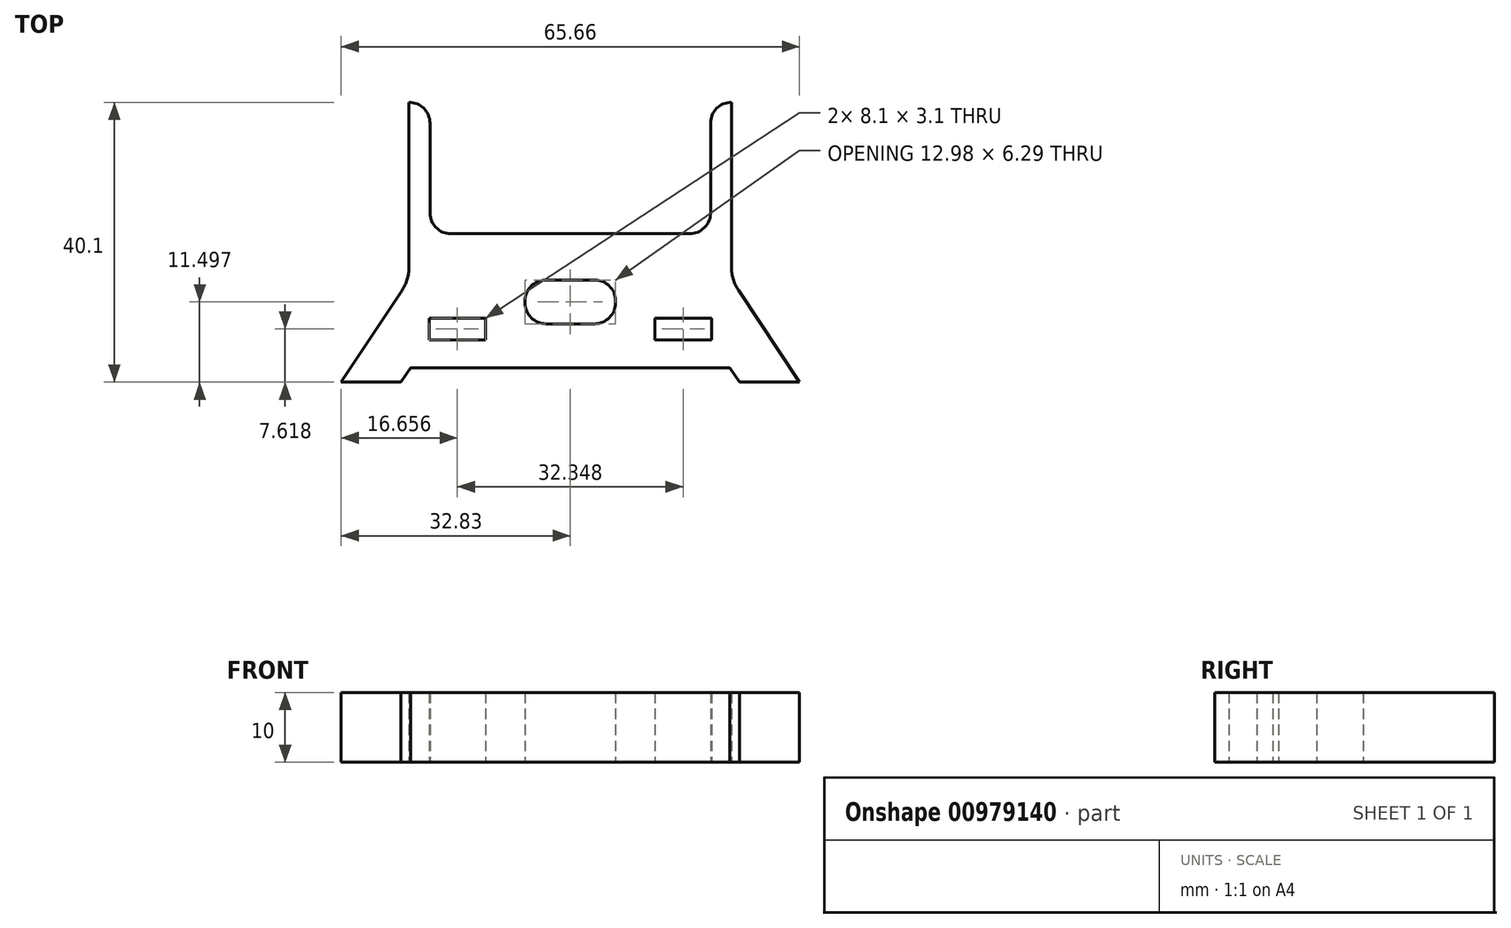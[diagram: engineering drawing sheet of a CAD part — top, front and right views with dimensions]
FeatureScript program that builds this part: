
annotation { "Feature Type Name" : "Feature", "Feature Type Description" : "" }
export const myFeature = defineFeature(function(context is Context, id is Id, definition is map)
    precondition{}
    {
        {
            var Q0;
            Q0=qCreatedBy(makeId("Top.planeOp"),FACE);
            var sketch = newSketch(context, id + "F0", { "sketchPlane" : qUnion([Q0])});
            skLineSegment(sketch, "E0.bottom", {"start": v(17.1, -18.83) * mm, "end": v(-17.1, -18.83) * mm});
            skLineSegment(sketch, "E0.left", {"start": v(20.1, -15.83) * mm, "end": v(20.1, -3) * mm});
            skLineSegment(sketch, "E0.right", {"start": v(-20.1, -15.83) * mm, "end": v(-20.1, -3) * mm});
            skPoint(sketch, "E0.middle", {"position": v(0, 0) * mm});
            skLineSegment(sketch, "E1.top", {"start": v(23.1, 25.45) * mm, "end": v(-23.1, 25.45) * mm});
            skLineSegment(sketch, "E1.left", {"start": v(23.1, -23.64) * mm, "end": v(23.1, 25.45) * mm});
            skLineSegment(sketch, "E1.right", {"start": v(-23.1, -23.64) * mm, "end": v(-23.1, 25.45) * mm});
            skPoint(sketch, "E2.startSnap0", {"position": v(-23.1, 0) * mm});
            skPoint(sketch, "E2.endSnap0", {"position": v(23.1, 0) * mm});
            skLineSegment(sketch, "E3", {"start": v(-24.1, -26.96) * mm, "end": v(-32.83, -40.1) * mm});
            skLineSegment(sketch, "E4", {"start": v(-32.83, -40.1) * mm, "end": v(-24.24, -40.1) * mm});
            skLineSegment(sketch, "E5", {"start": v(-24.24, -40.1) * mm, "end": v(-22.87, -38.03) * mm});
            skLineSegment(sketch, "E6", {"start": v(-22.87, -38.03) * mm, "end": v(0, -38.03) * mm});
            skLineSegment(sketch, "E7.MirrorCS", {"start": v(24.24, -40.1) * mm, "end": v(22.87, -38.03) * mm});
            skLineSegment(sketch, "E8.MirrorCS", {"start": v(22.87, -38.03) * mm, "end": v(0, -38.03) * mm});
            skLineSegment(sketch, "E9.MirrorCS", {"start": v(32.83, -40.1) * mm, "end": v(24.24, -40.1) * mm});
            skLineSegment(sketch, "E10.MirrorCS", {"start": v(24.1, -26.96) * mm, "end": v(32.83, -40.1) * mm});
            skLineSegment(sketch, "E11.bottom", {"start": v(-20.22, -30.93) * mm, "end": v(-12.12, -30.93) * mm});
            skLineSegment(sketch, "E11.top", {"start": v(-20.22, -34.03) * mm, "end": v(-12.12, -34.03) * mm});
            skLineSegment(sketch, "E11.left", {"start": v(-20.22, -30.93) * mm, "end": v(-20.22, -34.03) * mm});
            skLineSegment(sketch, "E11.right", {"start": v(-12.12, -30.93) * mm, "end": v(-12.12, -34.03) * mm});
            skLineSegment(sketch, "E12.MirrorCS", {"start": v(20.22, -30.93) * mm, "end": v(20.22, -34.03) * mm});
            skLineSegment(sketch, "E13.MirrorCS", {"start": v(20.22, -34.03) * mm, "end": v(12.12, -34.03) * mm});
            skLineSegment(sketch, "E14.MirrorCS", {"start": v(20.22, -30.93) * mm, "end": v(12.12, -30.93) * mm});
            skLineSegment(sketch, "E15.MirrorCS", {"start": v(12.12, -30.93) * mm, "end": v(12.12, -34.03) * mm});
            skLineSegment(sketch, "E16.bottom", {"start": v(-3.49, -25.46) * mm, "end": v(3.49, -25.46) * mm});
            skLineSegment(sketch, "E16.top", {"start": v(-3.49, -31.75) * mm, "end": v(3.49, -31.75) * mm});
            skLineSegment(sketch, "E16.left", {"start": v(-6.49, -28.46) * mm, "end": v(-6.49, -28.75) * mm});
            skLineSegment(sketch, "E16.right", {"start": v(6.49, -28.46) * mm, "end": v(6.49, -28.75) * mm});
            skPoint(sketch, "E16.middle", {"position": v(0, -28.6) * mm});
            skPoint(sketch, "E17.visualSharp", {"position": v(-6.49, -25.46) * mm});
            skArc(sketch, "E17.filletArc", {"start": v(-3.49, -25.46) * mm, "mid": v(-5.6, -26.34) * mm, "end": v(-6.49, -28.46) * mm});
            skPoint(sketch, "E18.visualSharp", {"position": v(6.49, -25.46) * mm});
            skArc(sketch, "E18.filletArc", {"start": v(6.49, -28.46) * mm, "mid": v(5.6, -26.34) * mm, "end": v(3.49, -25.46) * mm});
            skPoint(sketch, "E19.visualSharp", {"position": v(6.49, -31.75) * mm});
            skArc(sketch, "E19.filletArc", {"start": v(3.49, -31.75) * mm, "mid": v(5.6, -30.87) * mm, "end": v(6.49, -28.75) * mm});
            skPoint(sketch, "E20.visualSharp", {"position": v(-6.49, -31.75) * mm});
            skArc(sketch, "E20.filletArc", {"start": v(-6.49, -28.75) * mm, "mid": v(-5.6, -30.87) * mm, "end": v(-3.49, -31.75) * mm});
            skPoint(sketch, "E21.visualSharp", {"position": v(-23.1, -25.45) * mm});
            skArc(sketch, "E21.filletArc", {"start": v(-24.1, -26.96) * mm, "mid": v(-23.36, -25.37) * mm, "end": v(-23.1, -23.64) * mm});
            skPoint(sketch, "E22.visualSharp", {"position": v(23.1, -25.45) * mm});
            skArc(sketch, "E22.filletArc", {"start": v(23.1, -23.64) * mm, "mid": v(23.36, -25.37) * mm, "end": v(24.1, -26.96) * mm});
            skPoint(sketch, "E23.visualSharp", {"position": v(-20.1, -18.83) * mm});
            skArc(sketch, "E23.filletArc", {"start": v(-20.1, -15.83) * mm, "mid": v(-19.22, -17.96) * mm, "end": v(-17.1, -18.83) * mm});
            skPoint(sketch, "E24.visualSharp", {"position": v(20.1, -18.83) * mm});
            skArc(sketch, "E24.filletArc", {"start": v(17.1, -18.83) * mm, "mid": v(19.22, -17.96) * mm, "end": v(20.1, -15.83) * mm});
            skPoint(sketch, "E25.newPointA", {"position": v(33.69, 0) * mm});
            skArc(sketch, "E25.filletArc", {"start": v(-20.1, -3) * mm, "mid": v(-20.98, -0.88) * mm, "end": v(-23.1, 0) * mm});
            skLineSegment(sketch, "E26", {"start": v(23.1, 0) * mm, "end": v(23.1, 0) * mm});
            skPoint(sketch, "E27.newPointA", {"position": v(20.1, 0) * mm});
            skArc(sketch, "E27.filletArc", {"start": v(23.1, 0) * mm, "mid": v(20.98, -0.88) * mm, "end": v(20.1, -3) * mm});
            skLineSegment(sketch, "E28", {"start": v(-24.24, -40.1) * mm, "end": v(24.24, -40.1) * mm, "construction": true});
            skSolve(sketch);
        }
        {
            var Q0;
            Q0=makeQuery(id+"F0.imprint","IMPRINT",FACE,{"disambiguationData":[TD([[makeQuery(id+"F0.imprint","IMPRINT",EDGE,{"derivedFrom":sQuery(id+"F0.wireOp",EDGE,"E0.bottom")}),1.0]])]});
            extrude(context, id + "F1", {"entities" : qUnion([Q0]), "depth" : 10 * mm, "offsetDistance" : 25 * mm});
        }
    });
